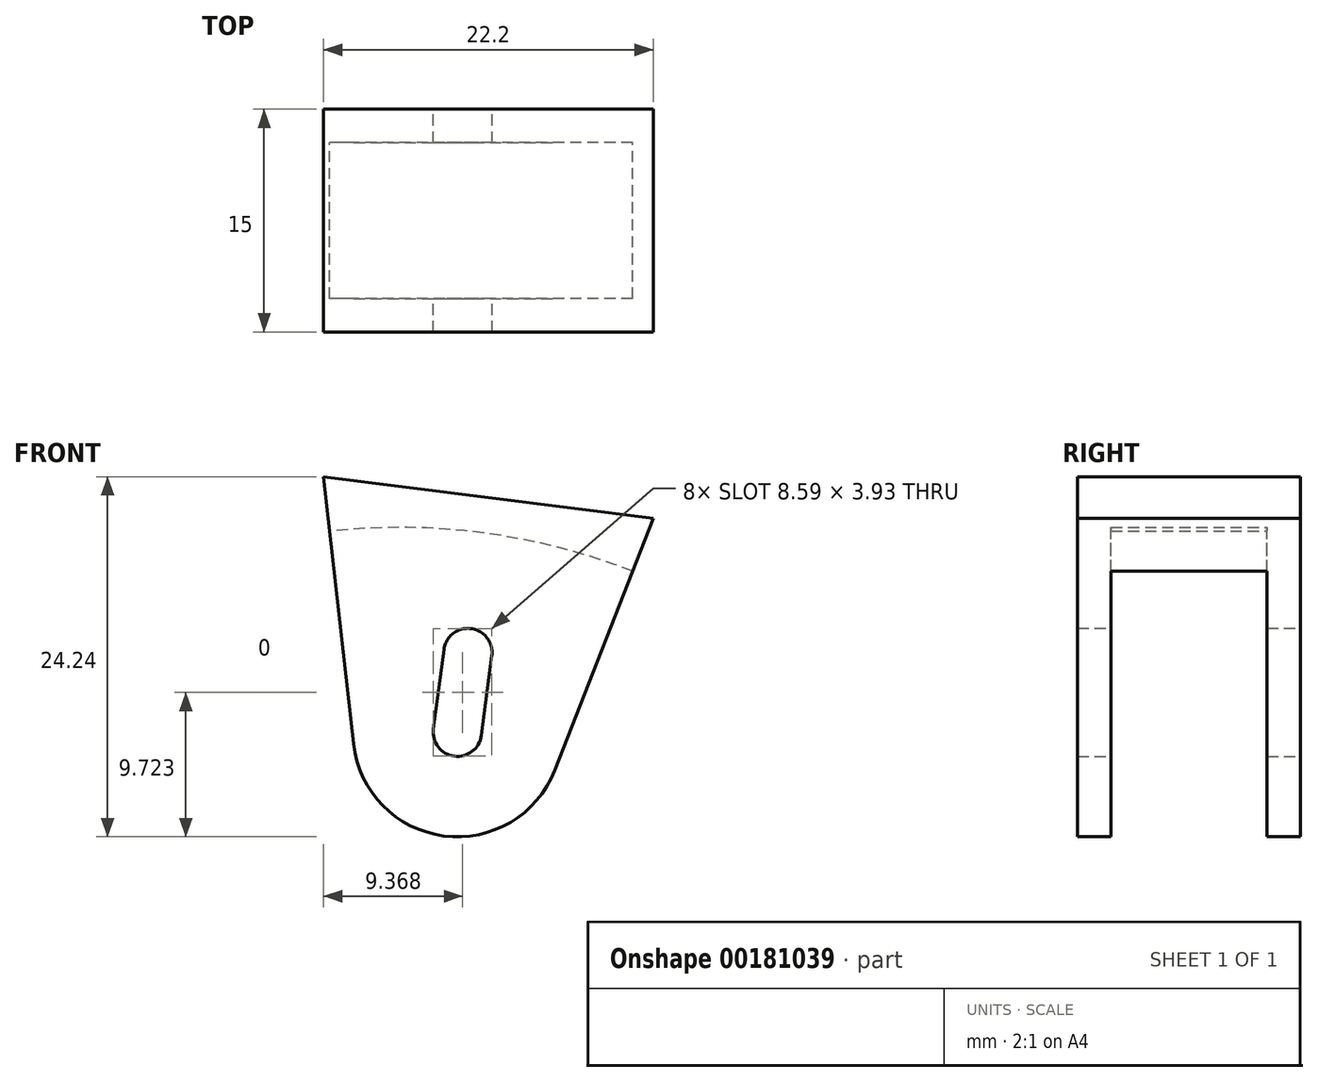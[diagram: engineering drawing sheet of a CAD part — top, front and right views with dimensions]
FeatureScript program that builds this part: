
annotation { "Feature Type Name" : "Feature", "Feature Type Description" : "" }
export const myFeature = defineFeature(function(context is Context, id is Id, definition is map)
    precondition{}
    {
        {
            var Q0;
            Q0=qCreatedBy(makeId("Front.planeOp"),FACE);
            var sketch = newSketch(context, id + "F0", { "sketchPlane" : qUnion([Q0])});
            skArc(sketch, "E0", {"start": v(9.4, 4.47) * mm, "mid": v(-0.64, 7.04) * mm, "end": v(-11, 7.15) * mm});
            skLineSegment(sketch, "E1", {"start": v(10.78, 8.01) * mm, "end": v(4.15, -8.94) * mm});
            skLineSegment(sketch, "E2", {"start": v(-11.42, 10.82) * mm, "end": v(10.78, 8.01) * mm});
            skLineSegment(sketch, "E3", {"start": v(-9.4, -7.16) * mm, "end": v(-11.42, 10.82) * mm});
            skArc(sketch, "E4", {"start": v(-9.4, -7.16) * mm, "mid": v(-3.32, -13.36) * mm, "end": v(4.15, -8.94) * mm});
            skLineSegment(sketch, "E5", {"start": v(-0.09, -1.22) * mm, "end": v(-0.8, -6.6) * mm});
            skArc(sketch, "E6", {"start": v(-0.09, -1.22) * mm, "mid": v(-1.49, 0.6) * mm, "end": v(-3.3, -0.8) * mm});
            skLineSegment(sketch, "E7", {"start": v(-4.02, -6.17) * mm, "end": v(-3.3, -0.8) * mm});
            skArc(sketch, "E8", {"start": v(-4.02, -6.17) * mm, "mid": v(-2.62, -8) * mm, "end": v(-0.8, -6.6) * mm});
            skSolve(sketch);
        }
        {
            var Q0;
            {var subQ0=sQuery(id+"F0.wireOp",EDGE,"E0");Q0=makeQuery(id+"F0.imprint","IMPRINT",FACE,{"disambiguationData":[TD([[makeQuery(id+"F0.imprint","IMPRINT",EDGE,{"derivedFrom":subQ0}),-1.0]])]});}
            var Q1;
            {var subQ2=sQuery(id+"F0.wireOp",EDGE,"E0");Q1=makeQuery(id+"F0.imprint","IMPRINT",FACE,{"disambiguationData":[TD([[makeQuery(id+"F0.imprint","IMPRINT",EDGE,{"derivedFrom":subQ2}),1.0]])]});}
            extrude(context, id + "F1", {"entities" : qUnion([Q0, Q1]), "endBound" : BoundingType.SYMMETRIC, "depth" : 15 * mm});
        }
        {
            var Q0;
            {var subQ2=sQuery(id+"F0.wireOp",EDGE,"E0");Q0=makeQuery(id+"F0.imprint","IMPRINT",FACE,{"disambiguationData":[TD([[makeQuery(id+"F0.imprint","IMPRINT",EDGE,{"derivedFrom":subQ2}),1.0]])]});}
            extrude(context, id + "F2", {"entities" : qUnion([Q0]), "operationType" : NewBodyOperationType.REMOVE, "endBound" : BoundingType.SYMMETRIC, "depth" : 10.5 * mm});
        }
    });
